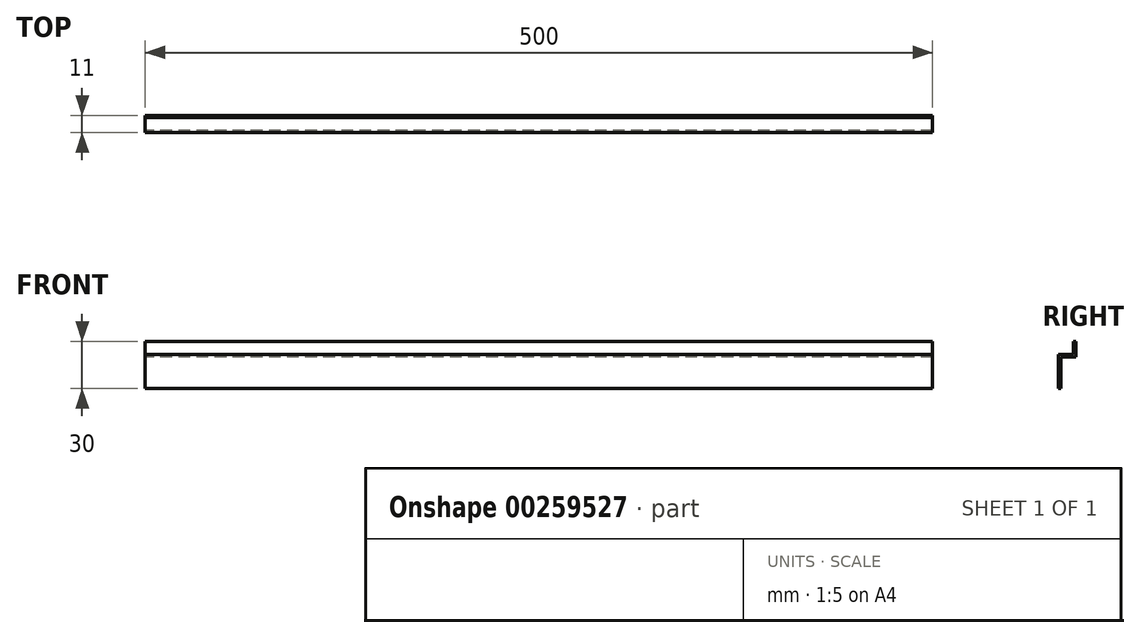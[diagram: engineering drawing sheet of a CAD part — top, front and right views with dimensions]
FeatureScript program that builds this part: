
annotation { "Feature Type Name" : "Feature", "Feature Type Description" : "" }
export const myFeature = defineFeature(function(context is Context, id is Id, definition is map)
    precondition{}
    {
        {
            var Q0;
            Q0=qCreatedBy(makeId("Right.planeOp"),FACE);
            var sketch = newSketch(context, id + "F0", { "sketchPlane" : qUnion([Q0])});
            skLineSegment(sketch, "E0", {"start": v(-28.14, 39.16) * mm, "end": v(-28.14, 29.16) * mm});
            skLineSegment(sketch, "E1", {"start": v(-37.64, 29.16) * mm, "end": v(-28.14, 29.16) * mm});
            skLineSegment(sketch, "E2", {"start": v(-37.64, 29.16) * mm, "end": v(-37.64, 9.16) * mm});
            skLineSegment(sketch, "E3", {"start": v(-37.64, 9.16) * mm, "end": v(-39.14, 9.16) * mm});
            skLineSegment(sketch, "E4", {"start": v(-39.14, 9.16) * mm, "end": v(-39.14, 30.66) * mm});
            skLineSegment(sketch, "E5", {"start": v(-28.14, 39.16) * mm, "end": v(-29.64, 39.16) * mm});
            skLineSegment(sketch, "E6", {"start": v(-29.64, 39.16) * mm, "end": v(-29.64, 30.66) * mm});
            skLineSegment(sketch, "E7", {"start": v(-39.14, 30.66) * mm, "end": v(-29.64, 30.66) * mm});
            skSolve(sketch);
        }
        {
            var Q0;
            Q0=makeQuery(id+"F0.imprint","IMPRINT",FACE,{"disambiguationData":[TD([[makeQuery(id+"F0.imprint","IMPRINT",EDGE,{"derivedFrom":sQuery(id+"F0.wireOp",EDGE,"E0")}),-1.0]])]});
            extrude(context, id + "F1", {"entities" : qUnion([Q0]), "depth" : 500 * mm});
        }
    });
